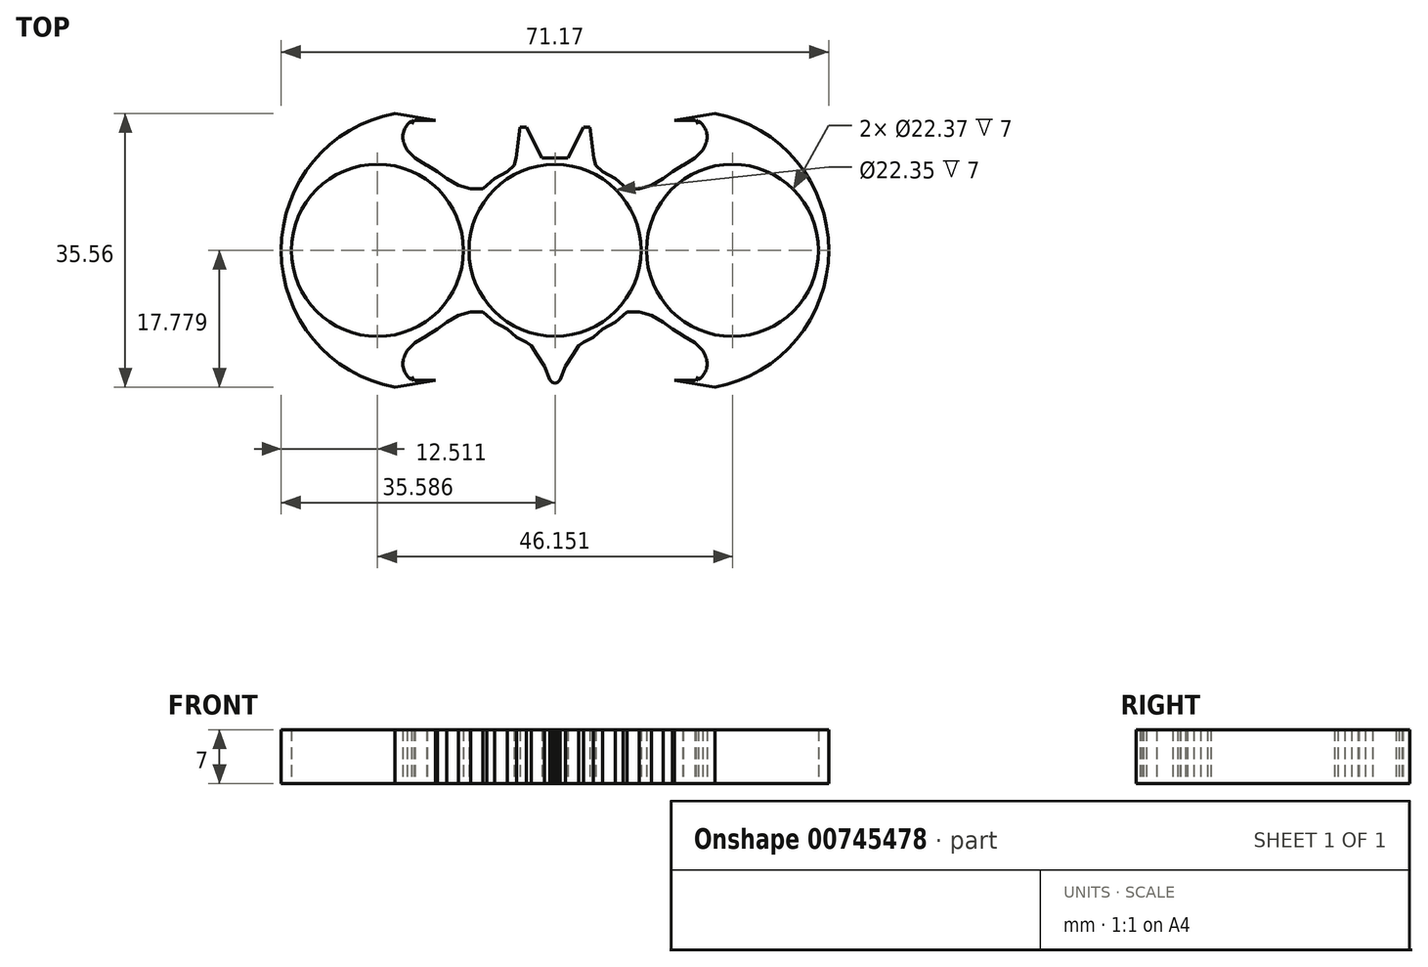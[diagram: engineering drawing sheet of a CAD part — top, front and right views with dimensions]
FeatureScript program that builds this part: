
annotation { "Feature Type Name" : "Feature", "Feature Type Description" : "" }
export const myFeature = defineFeature(function(context is Context, id is Id, definition is map)
    precondition{}
    {
        {
            var Q0;
            Q0=qCreatedBy(makeId("Top.planeOp"),FACE);
            var sketch = newSketch(context, id + "F0", { "sketchPlane" : qUnion([Q0])});
            skLineSegment(sketch, "E0", {"start": v(-11.2, 8.02) * mm, "end": v(-11.2, -20.99) * mm});
            skLineSegment(sketch, "E1", {"start": v(-11.2, 8.02) * mm, "end": v(-12.87, 8.02) * mm});
            skLineSegment(sketch, "E2", {"start": v(-12.87, 8.02) * mm, "end": v(-14.92, 12.02) * mm});
            skLineSegment(sketch, "E3", {"start": v(-14.92, 12.02) * mm, "end": v(-15.71, 12.02) * mm});
            skLineSegment(sketch, "E4", {"start": v(-15.71, 12.02) * mm, "end": v(-16.25, 8.02) * mm});
            skLineSegment(sketch, "E5", {"start": v(-16.25, 8.02) * mm, "end": v(-16.49, 7.07) * mm});
            skLineSegment(sketch, "E6", {"start": v(-16.49, 7.07) * mm, "end": v(-17.38, 6.25) * mm});
            skLineSegment(sketch, "E7", {"start": v(-17.38, 6.25) * mm, "end": v(-19.01, 5.37) * mm});
            skLineSegment(sketch, "E8", {"start": v(-19.01, 5.37) * mm, "end": v(-20.07, 4.47) * mm});
            skLineSegment(sketch, "E9", {"start": v(-20.07, 4.47) * mm, "end": v(-20.55, 4.02) * mm});
            skLineSegment(sketch, "E10", {"start": v(-20.55, 4.02) * mm, "end": v(-22.16, 4.02) * mm});
            skLineSegment(sketch, "E11", {"start": v(-22.16, 4.02) * mm, "end": v(-23.76, 4.47) * mm});
            skLineSegment(sketch, "E12", {"start": v(-23.76, 4.47) * mm, "end": v(-25.23, 5.37) * mm});
            skLineSegment(sketch, "E13", {"start": v(-25.23, 5.37) * mm, "end": v(-26.5, 6.25) * mm});
            skLineSegment(sketch, "E14", {"start": v(-26.5, 6.25) * mm, "end": v(-27.82, 7.07) * mm});
            skLineSegment(sketch, "E15", {"start": v(-27.82, 7.07) * mm, "end": v(-27.88, 7.1) * mm});
            skLineSegment(sketch, "E16", {"start": v(-27.88, 7.1) * mm, "end": v(-29.38, 8.02) * mm});
            skLineSegment(sketch, "E17", {"start": v(-29.38, 8.02) * mm, "end": v(-30.38, 9.02) * mm});
            skLineSegment(sketch, "E18", {"start": v(-30.38, 9.02) * mm, "end": v(-30.72, 9.68) * mm});
            skArc(sketch, "E19", {"start": v(-29.45, 13) * mm, "mid": v(-30.81, 11.62) * mm, "end": v(-30.72, 9.68) * mm});
            skLineSegment(sketch, "E20", {"start": v(-29.82, 12.43) * mm, "end": v(-29.45, 13) * mm});
            skLineSegment(sketch, "E21", {"start": v(-29.82, 12.43) * mm, "end": v(-29.82, 13.39) * mm});
            skLineSegment(sketch, "E22", {"start": v(-29.45, 12.89) * mm, "end": v(-29.82, 13.39) * mm});
            skLineSegment(sketch, "E23", {"start": v(-26.73, 12.89) * mm, "end": v(-29.45, 12.89) * mm});
            skLineSegment(sketch, "E24", {"start": v(-26.73, 12.89) * mm, "end": v(-31.98, 13.79) * mm});
            skArc(sketch, "E25", {"start": v(-31.98, 13.79) * mm, "mid": v(-46.78, -4) * mm, "end": v(-31.98, -21.77) * mm});
            skLineSegment(sketch, "E26", {"start": v(-46.78, -4) * mm, "end": v(-11.2, -4) * mm});
            skArc(sketch, "E27.MirrorCS", {"start": v(-29.45, -20.98) * mm, "mid": v(-30.81, -19.6) * mm, "end": v(-30.72, -17.66) * mm});
            skLineSegment(sketch, "E28.MirrorCS", {"start": v(-26.73, -20.87) * mm, "end": v(-31.98, -21.77) * mm});
            skLineSegment(sketch, "E29.MirrorCS", {"start": v(-26.73, -20.87) * mm, "end": v(-29.45, -20.87) * mm});
            skLineSegment(sketch, "E30.MirrorCS", {"start": v(-29.45, -20.87) * mm, "end": v(-29.82, -21.37) * mm});
            skLineSegment(sketch, "E31.MirrorCS", {"start": v(-29.82, -20.4) * mm, "end": v(-29.82, -21.37) * mm});
            skLineSegment(sketch, "E32.MirrorCS", {"start": v(-29.82, -20.4) * mm, "end": v(-29.45, -20.98) * mm});
            skLineSegment(sketch, "E33.MirrorCS", {"start": v(-30.38, -17) * mm, "end": v(-30.72, -17.66) * mm});
            skLineSegment(sketch, "E34.MirrorCS", {"start": v(-29.38, -16) * mm, "end": v(-30.38, -17) * mm});
            skLineSegment(sketch, "E35.MirrorCS", {"start": v(-27.88, -15.07) * mm, "end": v(-29.38, -16) * mm});
            skLineSegment(sketch, "E36.MirrorCS", {"start": v(-27.82, -15.05) * mm, "end": v(-27.88, -15.07) * mm});
            skLineSegment(sketch, "E37.MirrorCS", {"start": v(-26.5, -14.23) * mm, "end": v(-27.82, -15.05) * mm});
            skLineSegment(sketch, "E38.MirrorCS", {"start": v(-25.23, -13.35) * mm, "end": v(-26.5, -14.23) * mm});
            skLineSegment(sketch, "E39.MirrorCS", {"start": v(-23.76, -12.45) * mm, "end": v(-25.23, -13.35) * mm});
            skLineSegment(sketch, "E40.MirrorCS", {"start": v(-22.16, -12) * mm, "end": v(-23.76, -12.45) * mm});
            skLineSegment(sketch, "E41.MirrorCS", {"start": v(-20.55, -12) * mm, "end": v(-22.16, -12) * mm});
            skLineSegment(sketch, "E42.MirrorCS", {"start": v(-20.07, -12.45) * mm, "end": v(-20.55, -12) * mm});
            skLineSegment(sketch, "E43.MirrorCS", {"start": v(-19.01, -13.35) * mm, "end": v(-20.07, -12.45) * mm});
            skLineSegment(sketch, "E44.MirrorCS", {"start": v(-17.38, -14.23) * mm, "end": v(-19.01, -13.35) * mm});
            skLineSegment(sketch, "E45", {"start": v(-17.38, -14.23) * mm, "end": v(-16.18, -15.3) * mm});
            skLineSegment(sketch, "E46", {"start": v(-16.18, -15.3) * mm, "end": v(-14.9, -15.94) * mm});
            skLineSegment(sketch, "E47", {"start": v(-14.9, -15.94) * mm, "end": v(-14.25, -16.37) * mm});
            skLineSegment(sketch, "E48", {"start": v(-14.25, -16.37) * mm, "end": v(-13.49, -17.6) * mm});
            skLineSegment(sketch, "E49", {"start": v(-13.49, -17.6) * mm, "end": v(-12.59, -19.06) * mm});
            skLineSegment(sketch, "E50", {"start": v(-12.59, -19.06) * mm, "end": v(-11.86, -20.81) * mm});
            skLineSegment(sketch, "E51", {"start": v(-11.86, -20.81) * mm, "end": v(-11.68, -21) * mm});
            skLineSegment(sketch, "E52", {"start": v(-11.68, -21) * mm, "end": v(-11.54, -21.14) * mm});
            skLineSegment(sketch, "E53", {"start": v(-11.54, -21.14) * mm, "end": v(-11.38, -21.22) * mm});
            skLineSegment(sketch, "E54", {"start": v(-11.2, -20.99) * mm, "end": v(-11.2, -21.24) * mm});
            skLineSegment(sketch, "E55", {"start": v(-11.2, -21.24) * mm, "end": v(-11.38, -21.22) * mm});
            skLineSegment(sketch, "E56.MirrorCS", {"start": v(-3.37, -13.35) * mm, "end": v(-2.32, -12.45) * mm});
            skLineSegment(sketch, "E57.MirrorCS", {"start": v(7.06, -20.87) * mm, "end": v(7.43, -21.37) * mm});
            skLineSegment(sketch, "E58.MirrorCS", {"start": v(7.06, 12.89) * mm, "end": v(7.43, 13.39) * mm});
            skLineSegment(sketch, "E59.MirrorCS", {"start": v(-5, -14.23) * mm, "end": v(-3.37, -13.35) * mm});
            skLineSegment(sketch, "E60.MirrorCS", {"start": v(7.43, -20.4) * mm, "end": v(7.43, -21.37) * mm});
            skLineSegment(sketch, "E61.MirrorCS", {"start": v(-10.7, -21) * mm, "end": v(-10.84, -21.14) * mm});
            skLineSegment(sketch, "E62.MirrorCS", {"start": v(7.43, 12.43) * mm, "end": v(7.06, 13) * mm});
            skLineSegment(sketch, "E63.MirrorCS", {"start": v(-11.2, -21.24) * mm, "end": v(-11, -21.22) * mm});
            skLineSegment(sketch, "E64.MirrorCS", {"start": v(7.43, -20.4) * mm, "end": v(7.06, -20.98) * mm});
            skLineSegment(sketch, "E65.MirrorCS", {"start": v(-10.84, -21.14) * mm, "end": v(-11, -21.22) * mm});
            skLineSegment(sketch, "E66.MirrorCS", {"start": v(-10.52, -20.81) * mm, "end": v(-10.7, -21) * mm});
            skLineSegment(sketch, "E67.MirrorCS", {"start": v(7.43, 12.43) * mm, "end": v(7.43, 13.39) * mm});
            skLineSegment(sketch, "E68.MirrorCS", {"start": v(8, -17) * mm, "end": v(8.33, -17.66) * mm});
            skLineSegment(sketch, "E69.MirrorCS", {"start": v(4.1, 6.25) * mm, "end": v(5.44, 7.07) * mm});
            skLineSegment(sketch, "E70.MirrorCS", {"start": v(-8.9, -17.6) * mm, "end": v(-9.8, -19.06) * mm});
            skLineSegment(sketch, "E71.MirrorCS", {"start": v(4.1, -14.23) * mm, "end": v(5.44, -15.05) * mm});
            skLineSegment(sketch, "E72.MirrorCS", {"start": v(5.44, 7.07) * mm, "end": v(5.5, 7.1) * mm});
            skLineSegment(sketch, "E73.MirrorCS", {"start": v(-2.32, -12.45) * mm, "end": v(-1.84, -12) * mm});
            skLineSegment(sketch, "E74.MirrorCS", {"start": v(4.34, -20.87) * mm, "end": v(7.06, -20.87) * mm});
            skLineSegment(sketch, "E75.MirrorCS", {"start": v(-1.84, -12) * mm, "end": v(-0.23, -12) * mm});
            skLineSegment(sketch, "E76.MirrorCS", {"start": v(-2.32, 4.47) * mm, "end": v(-1.84, 4.02) * mm});
            skLineSegment(sketch, "E77.MirrorCS", {"start": v(-7.47, 12.02) * mm, "end": v(-6.67, 12.02) * mm});
            skLineSegment(sketch, "E78.MirrorCS", {"start": v(1.37, -12.45) * mm, "end": v(2.84, -13.35) * mm});
            skLineSegment(sketch, "E79.MirrorCS", {"start": v(-8.13, -16.37) * mm, "end": v(-8.9, -17.6) * mm});
            skLineSegment(sketch, "E80.MirrorCS", {"start": v(1.37, 4.47) * mm, "end": v(2.84, 5.37) * mm});
            skLineSegment(sketch, "E81.MirrorCS", {"start": v(2.84, 5.37) * mm, "end": v(4.1, 6.25) * mm});
            skLineSegment(sketch, "E82.MirrorCS", {"start": v(6.99, 8.02) * mm, "end": v(8, 9.02) * mm});
            skLineSegment(sketch, "E83.MirrorCS", {"start": v(4.34, 12.89) * mm, "end": v(9.6, 13.79) * mm});
            skLineSegment(sketch, "E84.MirrorCS", {"start": v(5.44, -15.05) * mm, "end": v(5.5, -15.07) * mm});
            skLineSegment(sketch, "E85.MirrorCS", {"start": v(4.34, 12.89) * mm, "end": v(7.06, 12.89) * mm});
            skLineSegment(sketch, "E86.MirrorCS", {"start": v(-7.5, -15.94) * mm, "end": v(-8.13, -16.37) * mm});
            skLineSegment(sketch, "E87.MirrorCS", {"start": v(4.34, -20.87) * mm, "end": v(9.6, -21.77) * mm});
            skLineSegment(sketch, "E88.MirrorCS", {"start": v(2.84, -13.35) * mm, "end": v(4.1, -14.23) * mm});
            skLineSegment(sketch, "E89.MirrorCS", {"start": v(8, 9.02) * mm, "end": v(8.33, 9.68) * mm});
            skLineSegment(sketch, "E90.MirrorCS", {"start": v(6.99, -16) * mm, "end": v(8, -17) * mm});
            skLineSegment(sketch, "E91.MirrorCS", {"start": v(-3.37, 5.37) * mm, "end": v(-2.32, 4.47) * mm});
            skLineSegment(sketch, "E92.MirrorCS", {"start": v(-5.9, 7.07) * mm, "end": v(-5, 6.25) * mm});
            skLineSegment(sketch, "E93.MirrorCS", {"start": v(-5, 6.25) * mm, "end": v(-3.37, 5.37) * mm});
            skLineSegment(sketch, "E94.MirrorCS", {"start": v(-6.14, 8.02) * mm, "end": v(-5.9, 7.07) * mm});
            skLineSegment(sketch, "E95.MirrorCS", {"start": v(-1.84, 4.02) * mm, "end": v(-0.23, 4.02) * mm});
            skLineSegment(sketch, "E96.MirrorCS", {"start": v(-5, -14.23) * mm, "end": v(-6.21, -15.3) * mm});
            skLineSegment(sketch, "E97.MirrorCS", {"start": v(-6.21, -15.3) * mm, "end": v(-7.5, -15.94) * mm});
            skArc(sketch, "E98.MirrorCS", {"start": v(7.06, -20.98) * mm, "mid": v(8.43, -19.6) * mm, "end": v(8.33, -17.66) * mm});
            skLineSegment(sketch, "E99.MirrorCS", {"start": v(-9.8, -19.06) * mm, "end": v(-10.52, -20.81) * mm});
            skLineSegment(sketch, "E100.MirrorCS", {"start": v(-11.2, 8.02) * mm, "end": v(-9.52, 8.02) * mm});
            skLineSegment(sketch, "E101.MirrorCS", {"start": v(-9.52, 8.02) * mm, "end": v(-7.47, 12.02) * mm});
            skLineSegment(sketch, "E102.MirrorCS", {"start": v(5.5, 7.1) * mm, "end": v(6.99, 8.02) * mm});
            skLineSegment(sketch, "E103.MirrorCS", {"start": v(-0.23, 4.02) * mm, "end": v(1.37, 4.47) * mm});
            skLineSegment(sketch, "E104.MirrorCS", {"start": v(-0.23, -12) * mm, "end": v(1.37, -12.45) * mm});
            skLineSegment(sketch, "E105.MirrorCS", {"start": v(24.39, -4) * mm, "end": v(-11.2, -4) * mm});
            skArc(sketch, "E106.MirrorCS", {"start": v(9.6, 13.79) * mm, "mid": v(24.39, -4) * mm, "end": v(9.6, -21.77) * mm});
            skArc(sketch, "E107.MirrorCS", {"start": v(7.06, 13) * mm, "mid": v(8.43, 11.62) * mm, "end": v(8.33, 9.68) * mm});
            skLineSegment(sketch, "E108.MirrorCS", {"start": v(5.5, -15.07) * mm, "end": v(6.99, -16) * mm});
            skLineSegment(sketch, "E109.MirrorCS", {"start": v(-6.67, 12.02) * mm, "end": v(-6.14, 8.02) * mm});
            skCircle(sketch, "E110", {"center": v(-11.2, -4) * mm, "radius": 11.18 * mm});
            skCircle(sketch, "E111", {"center": v(-34.27, -4) * mm, "radius": 11.19 * mm});
            skCircle(sketch, "E112.MirrorC", {"center": v(11.88, -4) * mm, "radius": 11.19 * mm});
            skSolve(sketch);
        }
        {
            var Q0;
            Q0 = qSketchRegion(id + "F0", true);
            extrude(context, id + "F1", {"entities" : qUnion([Q0]), "depth" : 7 * mm, "offsetDistance" : 25.4 * mm});
        }
    });
